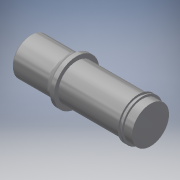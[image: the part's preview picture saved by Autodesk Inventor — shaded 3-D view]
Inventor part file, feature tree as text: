
AUTODESK INVENTOR PART (.ipt)
format: ipt  version: 2019 (Build 230136000, 136)  size: 156,672 bytes
history: native  units: mm
features: other x6, chamfer x2, fillet x1
ambient origin geometry x6: Origin, XZ Plane, XY Plane, X Axis, Y Axis, Z Axis
bodies: Body1 (feature_tree)
feature tree (9):
  other  "實體1"
  other  "迴轉1"
  chamfer  "倒角4"  [1 undecoded]
  chamfer  "倒角1"  Distance=9.0mm
  fillet  "圓角1"  Radius=11.0mm
  other  "扣環槽1"
  other  "起始平面"
  other  "主要草圖"
  other  "iFeature27:1"
note: 1 required parameter value undecoded (feature->parameter linkage not recoverable at this tier; creation-order binding heuristic only, values carry confidence <= 0.55)
